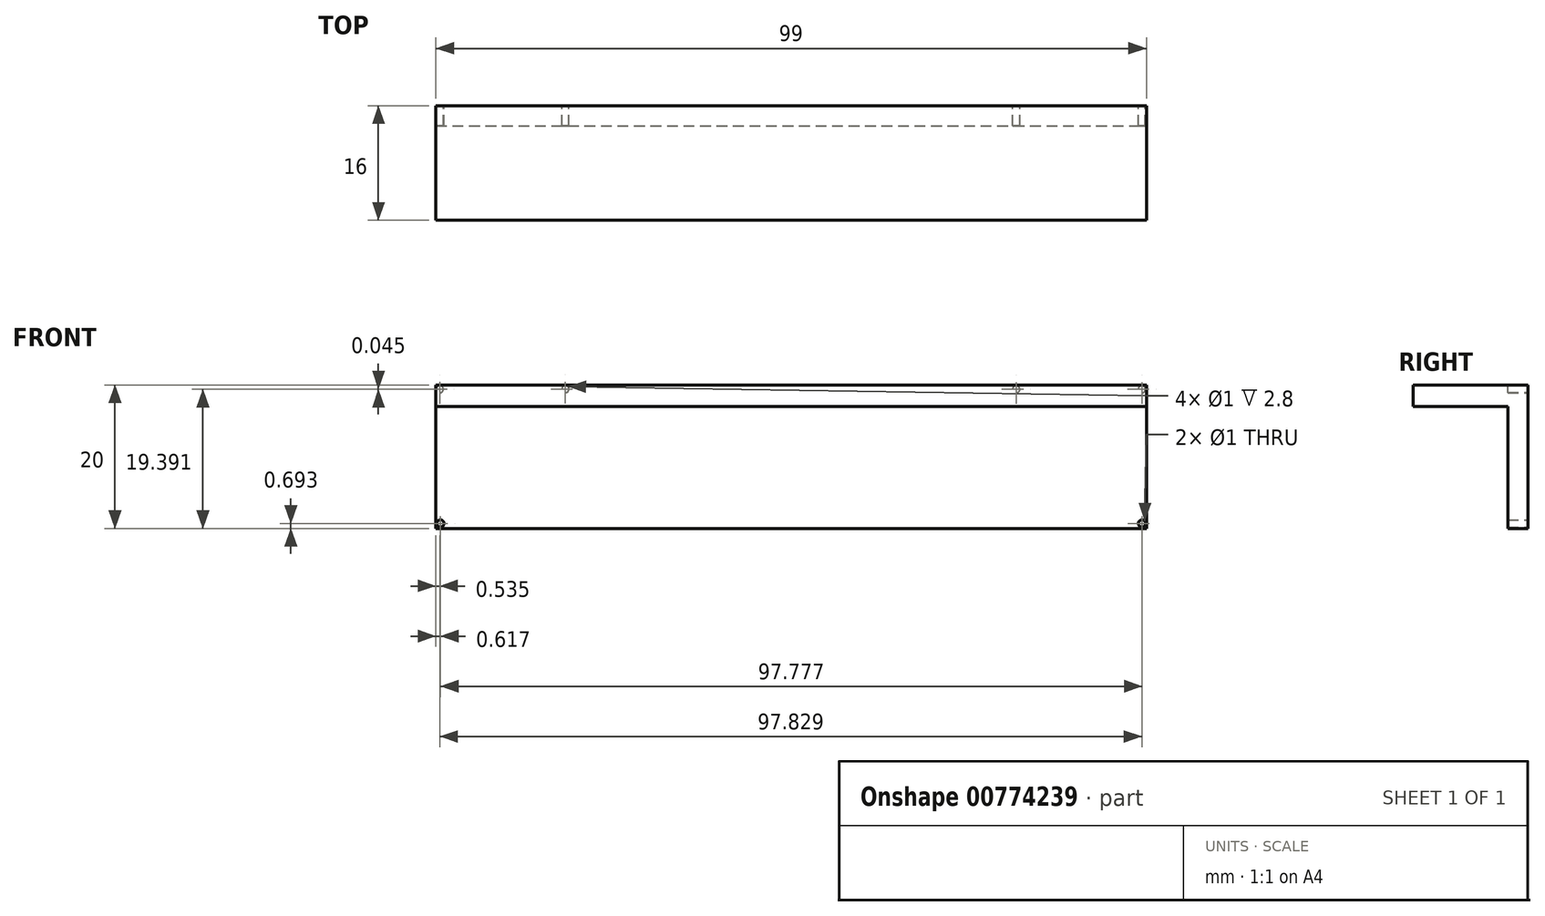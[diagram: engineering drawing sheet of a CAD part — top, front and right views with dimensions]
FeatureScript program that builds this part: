
annotation { "Feature Type Name" : "Feature", "Feature Type Description" : "" }
export const myFeature = defineFeature(function(context is Context, id is Id, definition is map)
    precondition{}
    {
        {
            var Q0;
            Q0=qCreatedBy(makeId("Front.planeOp"),FACE);
            var sketch = newSketch(context, id + "F0", { "sketchPlane" : qUnion([Q0])});
            skLineSegment(sketch, "E0.bottom", {"start": v(-71.95, 16.6) * mm, "end": v(27.05, 16.6) * mm});
            skLineSegment(sketch, "E0.top", {"start": v(-71.95, -3.4) * mm, "end": v(27.05, -3.4) * mm});
            skLineSegment(sketch, "E0.left", {"start": v(-71.95, 16.6) * mm, "end": v(-71.95, -3.4) * mm});
            skLineSegment(sketch, "E0.right", {"start": v(27.05, 16.6) * mm, "end": v(27.05, -3.4) * mm});
            skLineSegment(sketch, "E1", {"start": v(27.05, 13.6) * mm, "end": v(-71.95, 13.6) * mm});
            skSolve(sketch);
        }
        {
            var Q0;
            Q0=qSketchRegion(id+"F0",true);
            extrude(context, id + "F1", {"entities" : qUnion([Q0]), "depth" : 2.8 * mm, "offsetDistance" : 25 * mm});
        }
        {
            var Q0;
            {var subQ0=sQuery(id+"F0.wireOp",EDGE,"E0.bottom");Q0=makeQuery(id+"F0.imprint","IMPRINT",FACE,{"disambiguationData":[TD([[makeQuery(id+"F0.imprint","IMPRINT",EDGE,{"derivedFrom":subQ0}),-1.0]])]});}
            extrude(context, id + "F2", {"entities" : qUnion([Q0]), "operationType" : NewBodyOperationType.ADD, "depth" : 16 * mm, "offsetDistance" : 25 * mm});
        }
        {
            var Q0;
            {var subQ0=sQuery(id+"F0.wireOp",EDGE,"E0.top");Q0=makeQuery(id+"F0.imprint","IMPRINT",FACE,{"disambiguationData":[TD([[makeQuery(id+"F0.imprint","IMPRINT",EDGE,{"derivedFrom":subQ0}),1.0]])]});}
            var sketch = newSketch(context, id + "F3", { "sketchPlane" : qUnion([Q0])});
            skCircle(sketch, "E2", {"center": v(26.44, -2.7) * mm, "radius": 0.5 * mm});
            skCircle(sketch, "E3", {"center": v(-71.33, -2.7) * mm, "radius": 0.5 * mm});
            skSolve(sketch);
        }
        {
            var Q0;
            Q0 = qSketchRegion(id + "F3", true);
            extrude(context, id + "F4", {"entities" : qUnion([Q0]), "operationType" : NewBodyOperationType.REMOVE, "depth" : 3 * mm, "offsetDistance" : 25 * mm});
        }
        {
            var Q0;
            {var subQ0=sQuery(id+"F0.wireOp",EDGE,"E0.bottom");Q0=makeQuery(id+"F0.imprint","IMPRINT",FACE,{"disambiguationData":[TD([[makeQuery(id+"F0.imprint","IMPRINT",EDGE,{"derivedFrom":subQ0}),-1.0]])]});}
            var sketch = newSketch(context, id + "F5", { "sketchPlane" : qUnion([Q0])});
            skCircle(sketch, "E4", {"center": v(26.41, 16) * mm, "radius": 0.5 * mm});
            skCircle(sketch, "E5", {"center": v(-71.41, 16.01) * mm, "radius": 0.5 * mm});
            skCircle(sketch, "E6", {"center": v(8.91, 16) * mm, "radius": 0.5 * mm});
            skCircle(sketch, "E7", {"center": v(-53.91, 16.05) * mm, "radius": 0.5 * mm});
            skSolve(sketch);
        }
        {
            var Q0;
            Q0 = qSketchRegion(id + "F5", true);
            extrude(context, id + "F6", {"entities" : qUnion([Q0]), "operationType" : NewBodyOperationType.REMOVE, "depth" : 2.8 * mm, "offsetDistance" : 25 * mm});
        }
        {
            var Q0;
            Q0 = qSketchRegion(id + "F5", true);
            extrude(context, id + "F7", {"entities" : qUnion([Q0]), "operationType" : NewBodyOperationType.REMOVE, "oppositeDirection" : true, "depth" : 3 * mm, "offsetDistance" : 25 * mm});
        }
    });
